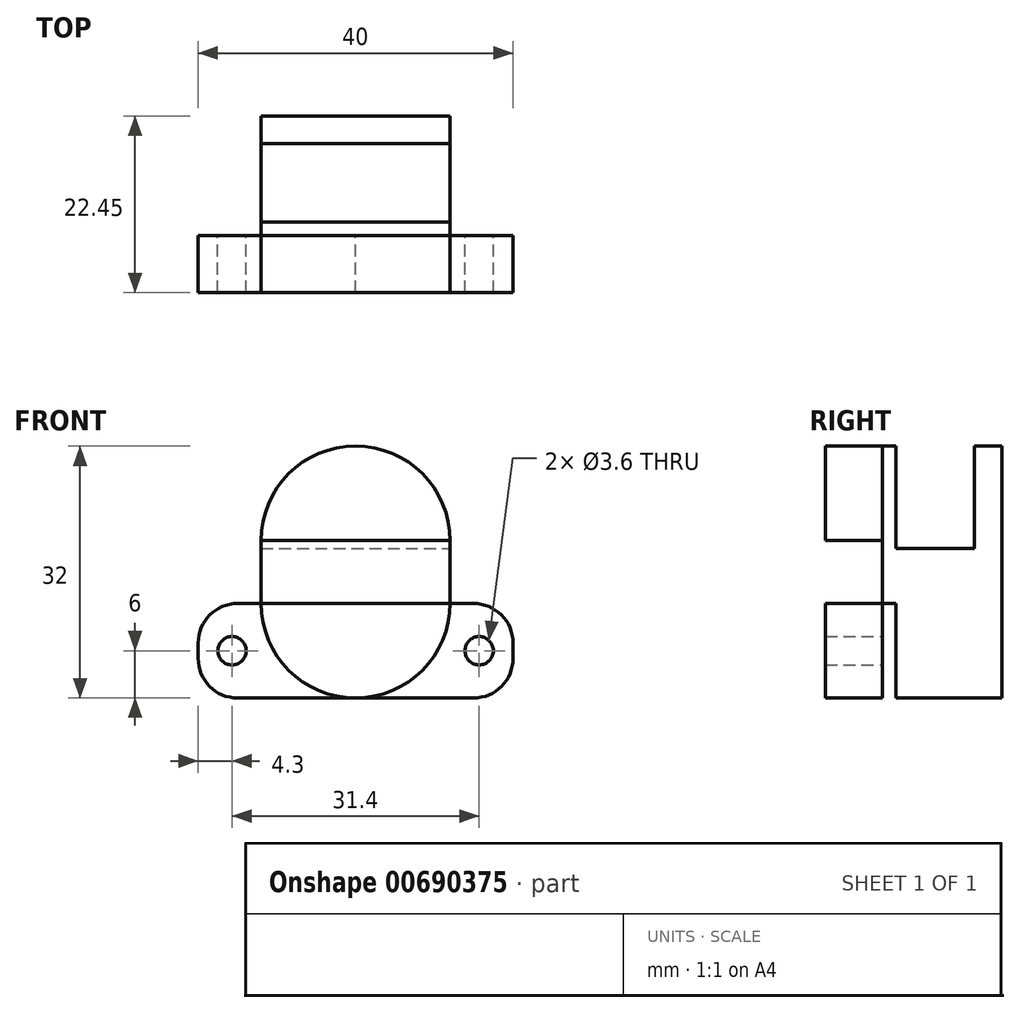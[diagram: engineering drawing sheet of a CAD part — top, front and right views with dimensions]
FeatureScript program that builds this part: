
annotation { "Feature Type Name" : "Feature", "Feature Type Description" : "" }
export const myFeature = defineFeature(function(context is Context, id is Id, definition is map)
    precondition{}
    {
        {
            var Q0;
            Q0=qCreatedBy(makeId("Front.planeOp"),FACE);
            var sketch = newSketch(context, id + "F0", { "sketchPlane" : qUnion([Q0])});
            skLineSegment(sketch, "E0.bottom", {"start": v(-20, 12) * mm, "end": v(20, 12) * mm});
            skLineSegment(sketch, "E0.top", {"start": v(-20, 0) * mm, "end": v(20, 0) * mm});
            skLineSegment(sketch, "E0.left", {"start": v(-20, 12) * mm, "end": v(-20, 0) * mm});
            skLineSegment(sketch, "E0.right", {"start": v(20, 12) * mm, "end": v(20, 0) * mm});
            skLineSegment(sketch, "E1", {"start": v(0, 20.86) * mm, "end": v(0, -29.6) * mm, "construction": true});
            skLineSegment(sketch, "E2", {"start": v(-12, 20) * mm, "end": v(12, 20) * mm});
            skArc(sketch, "E3", {"start": v(12, 20) * mm, "mid": v(0, 32) * mm, "end": v(-12, 20) * mm});
            skPoint(sketch, "E3.third.point", {"position": v(0, 32) * mm});
            skPoint(sketch, "E4.MirrorP", {"position": v(0, -26) * mm});
            skLineSegment(sketch, "E5", {"start": v(-12, 20) * mm, "end": v(-12, 12) * mm});
            skLineSegment(sketch, "E6", {"start": v(12, 20) * mm, "end": v(12, 12) * mm});
            skLineSegment(sketch, "E7", {"start": v(-31.4, 16) * mm, "end": v(45.65, 16) * mm, "construction": true});
            skLineSegment(sketch, "E8.MirrorCS", {"start": v(-12, 12) * mm, "end": v(12, 12) * mm});
            skArc(sketch, "E9.MirrorCS", {"start": v(12, 12) * mm, "mid": v(0, 0) * mm, "end": v(-12, 12) * mm});
            skSolve(sketch);
        }
        {
            var Q0;
            {var subQ0=sQuery(id+"F0.wireOp",EDGE,"E0.right");Q0=makeQuery(id+"F0.imprint","IMPRINT",FACE,{"disambiguationData":[TD([[makeQuery(id+"F0.imprint","IMPRINT",EDGE,{"derivedFrom":subQ0}),-1.0]])]});}
            var Q1;
            {var subQ0=sQuery(id+"F0.wireOp",EDGE,"E8.MirrorCS");Q1=makeQuery(id+"F0.imprint","IMPRINT",FACE,{"disambiguationData":[TD([[makeQuery(id+"F0.imprint","IMPRINT",EDGE,{"derivedFrom":subQ0}),-1.0]])]});}
            var Q2;
            {var subQ0=sQuery(id+"F0.wireOp",EDGE,"E0.left");Q2=makeQuery(id+"F0.imprint","IMPRINT",FACE,{"disambiguationData":[TD([[makeQuery(id+"F0.imprint","IMPRINT",EDGE,{"derivedFrom":subQ0}),1.0]])]});}
            var Q3;
            Q3=makeQuery(id+"F0.imprint","IMPRINT",FACE,{"disambiguationData":[TD([[makeQuery(id+"F0.imprint","IMPRINT",EDGE,{"derivedFrom":sQuery(id+"F0.wireOp",EDGE,"E2")}),1.0]])]});
            extrude(context, id + "F1", {"entities" : qUnion([Q0, Q1, Q2, Q3]), "depth" : 7.25 * mm, "offsetDistance" : 25 * mm});
        }
        {
            var Q0;
            Q0=makeQuery(id+"F0.imprint","IMPRINT",FACE,{"disambiguationData":[TD([[makeQuery(id+"F0.imprint","IMPRINT",EDGE,{"derivedFrom":sQuery(id+"F0.wireOp",EDGE,"E2")}),1.0]])]});
            var Q1;
            Q1=makeQuery(id+"F0.imprint","IMPRINT",FACE,{"disambiguationData":[TD([[makeQuery(id+"F0.imprint","IMPRINT",EDGE,{"derivedFrom":sQuery(id+"F0.wireOp",EDGE,"E2")}),-1.0]])]});
            var Q2;
            {var subQ0=sQuery(id+"F0.wireOp",EDGE,"E8.MirrorCS");Q2=makeQuery(id+"F0.imprint","IMPRINT",FACE,{"disambiguationData":[TD([[makeQuery(id+"F0.imprint","IMPRINT",EDGE,{"derivedFrom":subQ0}),-1.0]])]});}
            extrude(context, id + "F2", {"entities" : qUnion([Q0, Q1, Q2]), "oppositeDirection" : true, "depth" : 1.7 * mm, "offsetDistance" : 25 * mm});
        }
        {
            var Q0;
            Q0=makeQuery(id+"F2.opExtrude","CAP_FACE",FACE,{"disambiguationData":[OSD([sQuery(id+"F0.wireOp",EDGE,"E3"),sQuery(id+"F0.wireOp",EDGE,"E5"),sQuery(id+"F0.wireOp",EDGE,"E6"),sQuery(id+"F0.wireOp",EDGE,"E9.MirrorCS")])],"isStart":false});
            var sketch = newSketch(context, id + "F3", { "sketchPlane" : qUnion([Q0])});
            skLineSegment(sketch, "E10.0", {"start": v(12, 12) * mm, "end": v(-12, 12) * mm});
            skArc(sketch, "E10.1", {"start": v(-12, 12) * mm, "mid": v(0, 0) * mm, "end": v(12, 12) * mm});
            skSolve(sketch);
        }
        {
            var Q0;
            Q0=qSketchRegion(id+"F3",true);
            extrude(context, id + "F4", {"entities" : qUnion([Q0]), "operationType" : NewBodyOperationType.ADD, "depth" : 10 * mm, "offsetDistance" : 25 * mm});
        }
        {
            var Q0;
            Q0=makeQuery(id+"F4.opExtrude","CAP_FACE",FACE,{"disambiguationData":[OSD([sQuery(id+"F3.wireOp",EDGE,"E10.0"),sQuery(id+"F3.wireOp",EDGE,"E10.1")])],"isStart":false});
            var sketch = newSketch(context, id + "F5", { "sketchPlane" : qUnion([Q0])});
            skLineSegment(sketch, "E11.0", {"start": v(-12, 20) * mm, "end": v(-12, 12) * mm});
            skLineSegment(sketch, "E11.1", {"start": v(12, 20) * mm, "end": v(12, 12) * mm});
            skArc(sketch, "E11.2", {"start": v(-12, 20) * mm, "mid": v(0, 32) * mm, "end": v(12, 20) * mm});
            skArc(sketch, "E11.3", {"start": v(-12, 12) * mm, "mid": v(0, 0) * mm, "end": v(12, 12) * mm});
            skSolve(sketch);
        }
        {
            var Q0;
            Q0=qSketchRegion(id+"F5",true);
            extrude(context, id + "F6", {"entities" : qUnion([Q0]), "operationType" : NewBodyOperationType.ADD, "depth" : 3.5 * mm, "offsetDistance" : 25 * mm});
        }
        {
            var Q0;
            Q0=makeQuery(id+"F1.opExtrude","SWEPT_EDGE",EDGE,{"disambiguationData":[OSD([sQuery(id+"F0.wireOp",EDGE,"E0.bottom"),sQuery(id+"F0.wireOp",EDGE,"E0.left")])]});
            var Q1;
            Q1=makeQuery(id+"F1.opExtrude","SWEPT_EDGE",EDGE,{"disambiguationData":[OSD([sQuery(id+"F0.wireOp",EDGE,"E0.top"),sQuery(id+"F0.wireOp",EDGE,"E0.left")])]});
            var Q2;
            Q2=makeQuery(id+"F1.opExtrude","SWEPT_EDGE",EDGE,{"disambiguationData":[OSD([sQuery(id+"F0.wireOp",EDGE,"E0.bottom"),sQuery(id+"F0.wireOp",EDGE,"E0.right")])]});
            var Q3;
            Q3=makeQuery(id+"F1.opExtrude","SWEPT_EDGE",EDGE,{"disambiguationData":[OSD([sQuery(id+"F0.wireOp",EDGE,"E0.top"),sQuery(id+"F0.wireOp",EDGE,"E0.right")])]});
            fillet(context, id + "F7", {"entities" : qUnion([Q0, Q1, Q2, Q3]), "radius" : 5 * mm, "tangentPropagation" : true, "allowEdgeOverflow" : false});
        }
        {
            var Q0;
            {var subQ0=sQuery(id+"F0.wireOp",EDGE,"E0.right");Q0=makeQuery(id+"F0.imprint","IMPRINT",FACE,{"disambiguationData":[TD([[makeQuery(id+"F0.imprint","IMPRINT",EDGE,{"derivedFrom":subQ0}),-1.0]])]});}
            var sketch = newSketch(context, id + "F8", { "sketchPlane" : qUnion([Q0])});
            skCircle(sketch, "E12", {"center": v(15.7, 6) * mm, "radius": 1.8 * mm});
            skCircle(sketch, "E13.MirrorC", {"center": v(-15.7, 6) * mm, "radius": 1.8 * mm});
            skLineSegment(sketch, "E14", {"start": v(17.5, 10.05) * mm, "end": v(17.5, -2.1) * mm, "construction": true});
            skLineSegment(sketch, "E15.MirrorCS", {"start": v(-17.5, 10.05) * mm, "end": v(-17.5, -2.1) * mm, "construction": true});
            skLineSegment(sketch, "E16", {"start": v(-21.54, 6) * mm, "end": v(20.26, 6) * mm, "construction": true});
            skSolve(sketch);
        }
        {
            var Q0;
            Q0=sQuery(id+"F8.wireOp",VERTEX,"E12.center");
            var Q1;
            Q1=sQuery(id+"F8.wireOp",VERTEX,"E13.MirrorC.center");
            var Q2;
            Q2=makeQuery(id+"F1.opExtrude","SWEPT_BODY",BODY,{"disambiguationData":[OSD([sQuery(id+"F0.wireOp",EDGE,"E0.bottom"),sQuery(id+"F0.wireOp",EDGE,"E0.top"),sQuery(id+"F0.wireOp",EDGE,"E0.left"),sQuery(id+"F0.wireOp",EDGE,"E0.right"),sQuery(id+"F0.wireOp",EDGE,"E8.MirrorCS")])]});
            hole(context, id + "F9", {"style" : HoleStyle.SIMPLE, "endStyle" : HoleEndStyle.THROUGH, "oppositeDirection" : true, "holeDiameter" : 3.6 * mm, "majorDiameter" : 5 * mm, "isTappedThrough" : true, "tappedDepth" : 12 * mm, "tapClearance" : 3, "locations" : qUnion([Q0, Q1]), "scope" : qUnion([Q2])});
        }
        {
            var Q0;
            Q0=makeQuery(id+"F4.opExtrude","SWEPT_FACE",FACE,{"disambiguationData":[OSD([sQuery(id+"F3.wireOp",EDGE,"E10.0")])]});
            extrude(context, id + "F10", {"entities" : qUnion([Q0]), "operationType" : NewBodyOperationType.ADD, "depth" : 7 * mm, "offsetDistance" : 25 * mm});
        }
    });
